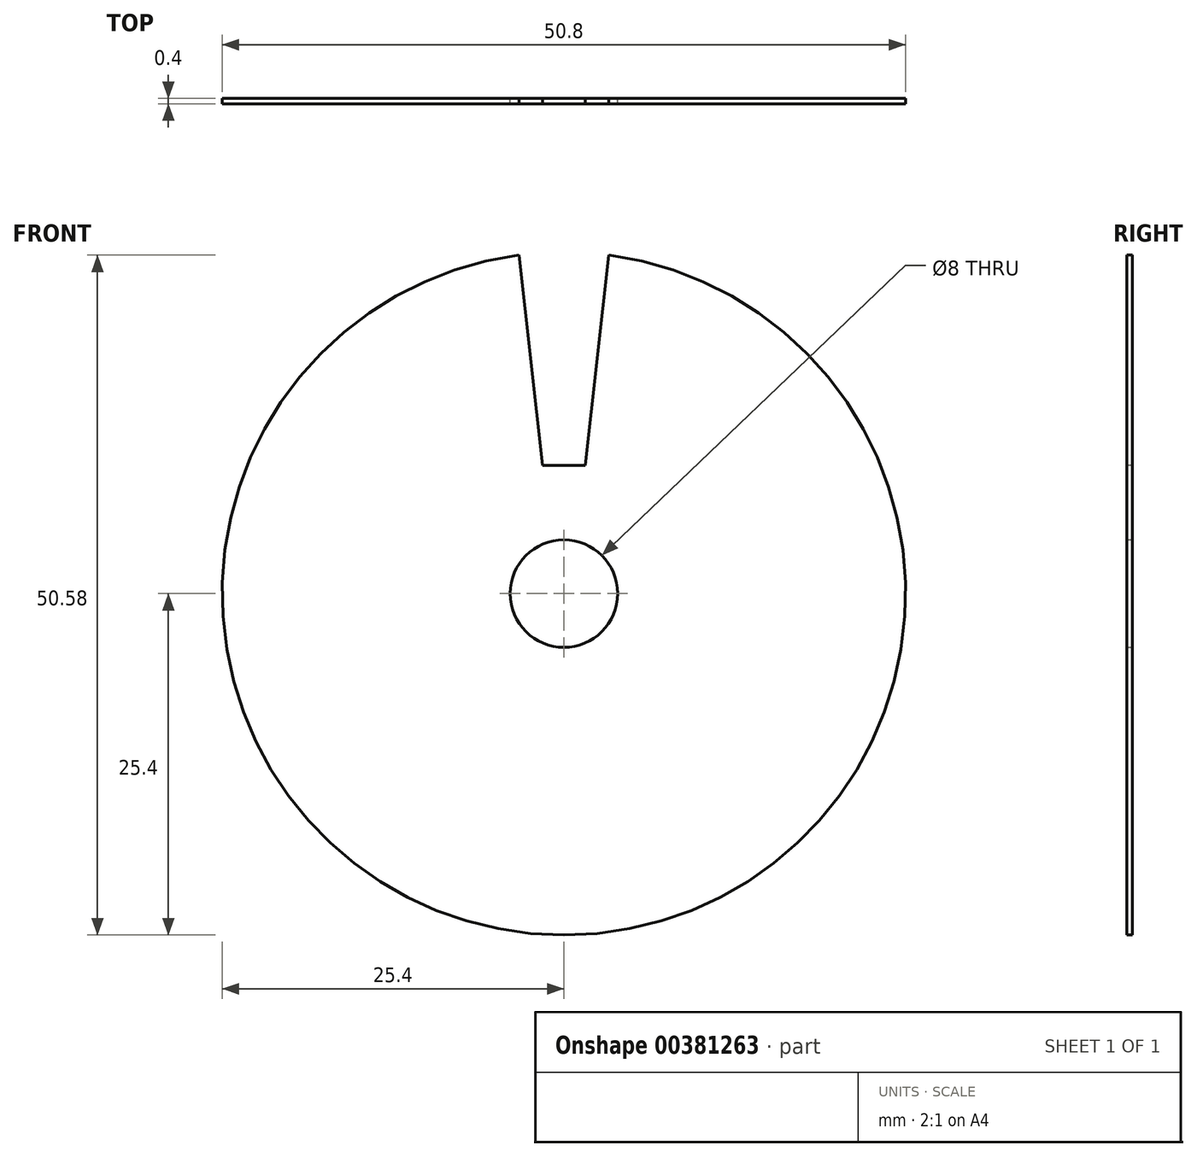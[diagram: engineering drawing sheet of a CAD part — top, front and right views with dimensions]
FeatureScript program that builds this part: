
annotation { "Feature Type Name" : "Feature", "Feature Type Description" : "" }
export const myFeature = defineFeature(function(context is Context, id is Id, definition is map)
    precondition{}
    {
        {
            var Q0;
            Q0=qCreatedBy(makeId("Front.planeOp"),FACE);
            var sketch = newSketch(context, id + "F0", { "sketchPlane" : qUnion([Q0])});
            skCircle(sketch, "E0", {"center": v(0, 0) * mm, "radius": 25.4 * mm});
            skCircle(sketch, "E1", {"center": v(0, 0) * mm, "radius": 4 * mm});
            skSolve(sketch);
        }
        {
            var Q0;
            Q0=qSketchRegion(id+"F0",true);
            extrude(context, id + "F1", {"entities" : qUnion([Q0]), "endBound" : BoundingType.SYMMETRIC, "depth" : 0.4 * mm});
        }
        {
            var Q0;
            Q0=makeQuery(id+"F1.opExtrude","CAP_FACE",FACE,{"disambiguationData":[OSD([sQuery(id+"F0.wireOp",EDGE,"E0"),sQuery(id+"F0.wireOp",EDGE,"E1")])],"isStart":false});
            var sketch = newSketch(context, id + "F2", { "sketchPlane" : qUnion([Q0])});
            skLineSegment(sketch, "E2.top", {"start": v(1.59, 9.53) * mm, "end": v(-1.59, 9.53) * mm});
            skPoint(sketch, "E2.middle", {"position": v(0, 55.57) * mm});
            skLineSegment(sketch, "E3", {"start": v(-3.32, 25.18) * mm, "end": v(0, 29.9) * mm});
            skLineSegment(sketch, "E4", {"start": v(0, 29.9) * mm, "end": v(3.32, 25.18) * mm});
            skPoint(sketch, "E5.orphan", {"position": v(0, 9.53) * mm});
            skPoint(sketch, "E2.right.start.orphan", {"position": v(-1.59, 101.62) * mm});
            skPoint(sketch, "E2.left.start.orphan", {"position": v(1.59, 101.62) * mm});
            skLineSegment(sketch, "E6", {"start": v(-1.59, 9.53) * mm, "end": v(-3.32, 25.18) * mm});
            skLineSegment(sketch, "E7", {"start": v(1.59, 9.52) * mm, "end": v(3.32, 25.18) * mm});
            skLineSegment(sketch, "E8", {"start": v(0, 0) * mm, "end": v(0, 9.53) * mm, "construction": true});
            skSolve(sketch);
        }
        {
            var Q0;
            Q0=qSketchRegion(id+"F2",true);
            extrude(context, id + "F3", {"entities" : qUnion([Q0]), "operationType" : NewBodyOperationType.REMOVE, "oppositeDirection" : true, "depth" : 25.4 * mm});
        }
    });
